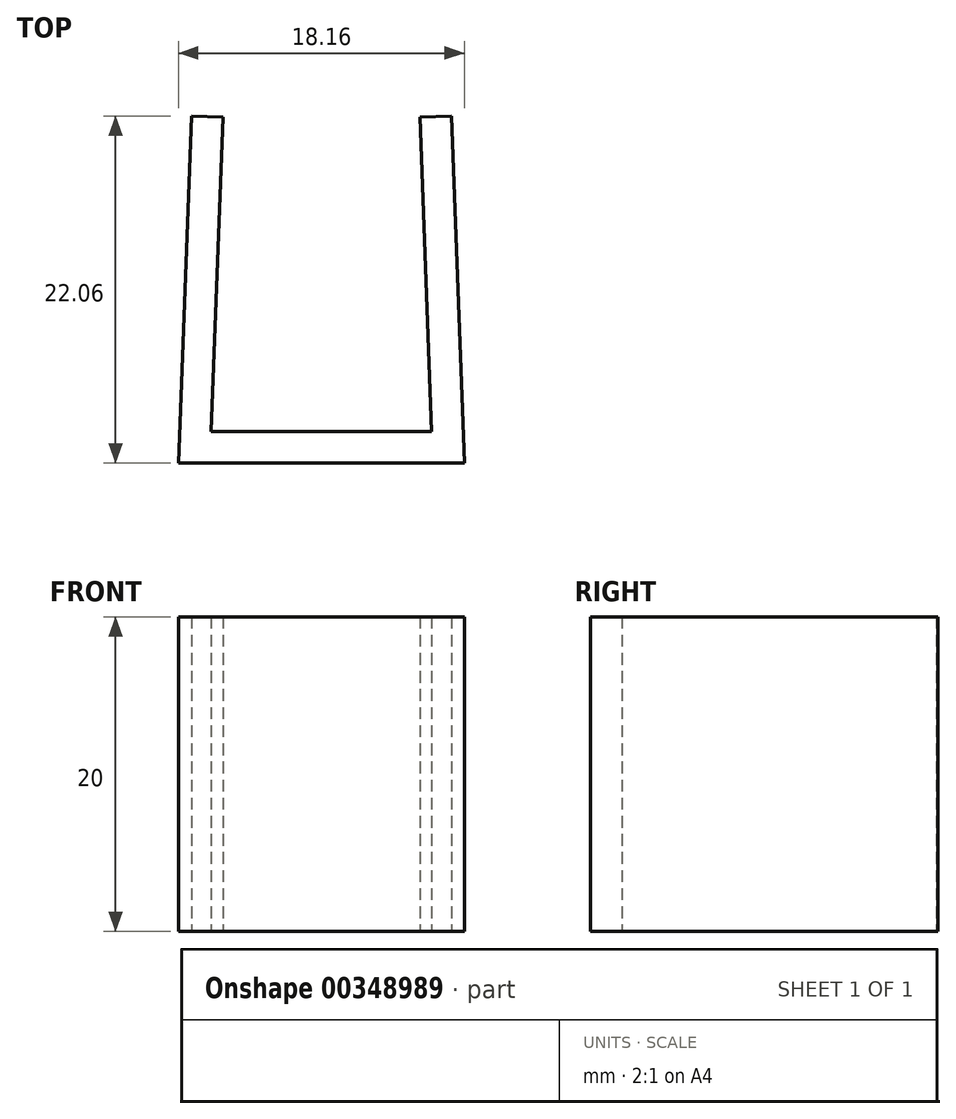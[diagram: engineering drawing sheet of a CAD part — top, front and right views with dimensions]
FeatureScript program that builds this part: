
annotation { "Feature Type Name" : "Feature", "Feature Type Description" : "" }
export const myFeature = defineFeature(function(context is Context, id is Id, definition is map)
    precondition{}
    {
        {
            var Q0;
            Q0=qCreatedBy(makeId("Top.planeOp"),FACE);
            var sketch = newSketch(context, id + "F0", { "sketchPlane" : qUnion([Q0])});
            skLineSegment(sketch, "E0", {"start": v(0, 0) * mm, "end": v(7, 0) * mm});
            skLineSegment(sketch, "E1", {"start": v(7, 0) * mm, "end": v(6.25, 19.99) * mm});
            skLineSegment(sketch, "E2.MirrorCS", {"start": v(0, 0) * mm, "end": v(-7, 0) * mm});
            skLineSegment(sketch, "E3.MirrorCS", {"start": v(-7, 0) * mm, "end": v(-6.25, 19.99) * mm});
            skLineSegment(sketch, "E4.0", {"start": v(-9.08, -2) * mm, "end": v(-8.25, 20.06) * mm});
            skLineSegment(sketch, "E4.1", {"start": v(0, -2) * mm, "end": v(-9.08, -2) * mm});
            skLineSegment(sketch, "E4.2", {"start": v(0, -2) * mm, "end": v(9.08, -2) * mm});
            skLineSegment(sketch, "E4.3", {"start": v(9.08, -2) * mm, "end": v(8.25, 20.06) * mm});
            skLineSegment(sketch, "E5", {"start": v(-8.25, 20.06) * mm, "end": v(-6.25, 19.99) * mm});
            skLineSegment(sketch, "E6", {"start": v(6.25, 19.99) * mm, "end": v(8.25, 20.06) * mm});
            skSolve(sketch);
        }
        {
            var Q0;
            Q0=makeQuery(id+"F0.imprint","IMPRINT",FACE,{"disambiguationData":[TD([[makeQuery(id+"F0.imprint","IMPRINT",EDGE,{"derivedFrom":sQuery(id+"F0.wireOp",EDGE,"E0")}),-1.0]])]});
            extrude(context, id + "F1", {"entities" : qUnion([Q0]), "depth" : 20 * mm});
        }
    });
